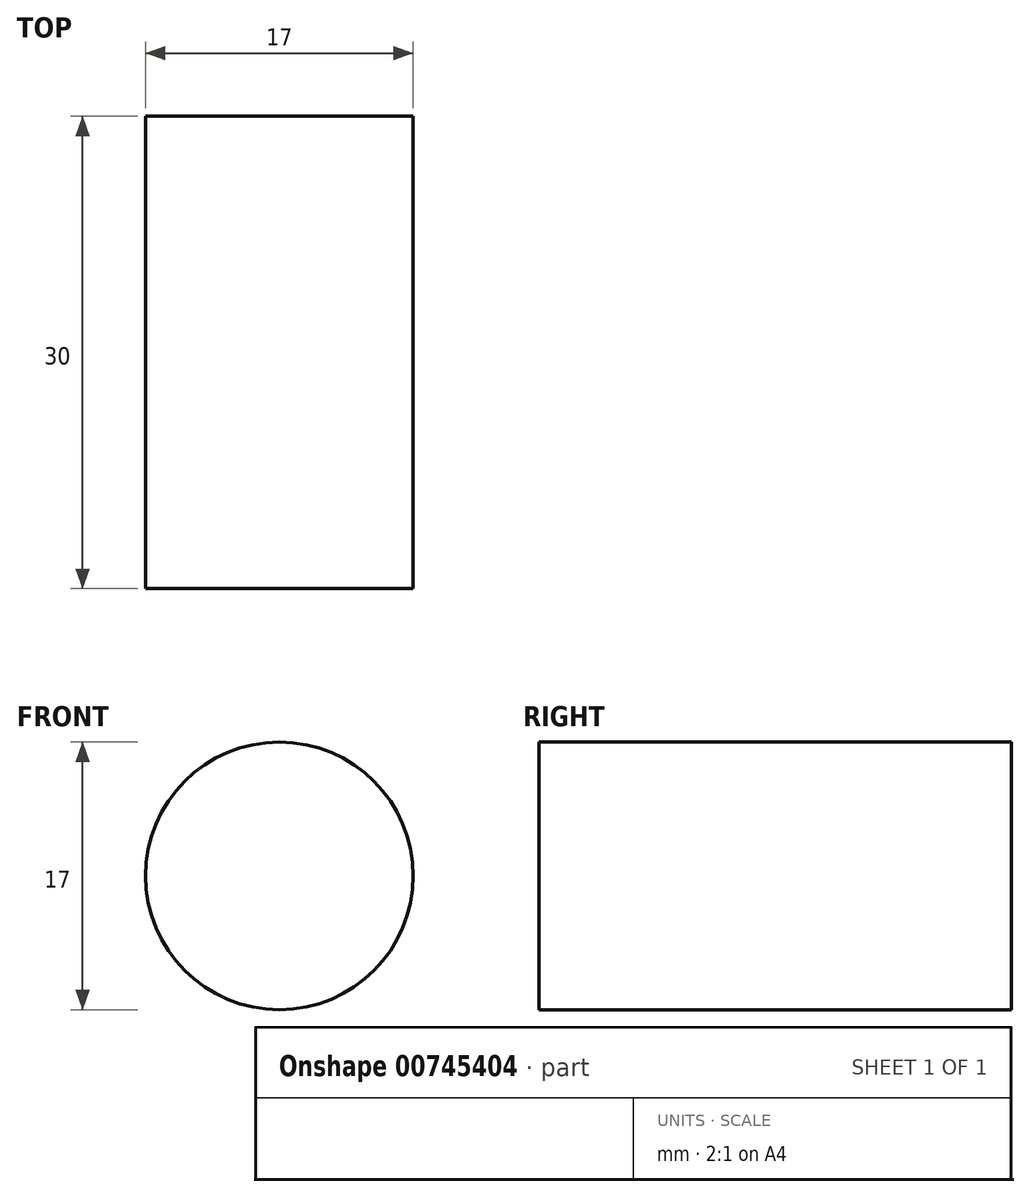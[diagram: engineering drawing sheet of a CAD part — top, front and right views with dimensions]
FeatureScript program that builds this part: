
annotation { "Feature Type Name" : "Feature", "Feature Type Description" : "" }
export const myFeature = defineFeature(function(context is Context, id is Id, definition is map)
    precondition{}
    {
        {
            var Q0;
            Q0=qCreatedBy(makeId("Front.planeOp"),FACE);
            var sketch = newSketch(context, id + "F0", { "sketchPlane" : qUnion([Q0])});
            skCircle(sketch, "E0", {"center": v(0, 0) * mm, "radius": 8.5 * mm});
            skLineSegment(sketch, "E1", {"start": v(0, 0) * mm, "end": v(100, 0) * mm, "construction": true});
            skSolve(sketch);
        }
        {
            var Q0;
            Q0 = qSketchRegion(id + "F0", true);
            extrude(context, id + "F1", {"entities" : qUnion([Q0]), "endBound" : BoundingType.SYMMETRIC, "depth" : 60 * mm, "offsetDistance" : 25 * mm});
        }
        {
            var Q0;
            Q0=qCreatedBy(makeId("Front.planeOp"),FACE);
            var sketch = newSketch(context, id + "F2", { "sketchPlane" : qUnion([Q0])});
            skCircle(sketch, "E2", {"center": v(0, 0) * mm, "radius": 13.32 * mm});
            skSolve(sketch);
        }
        {
            var Q0;
            Q0=makeQuery(id+"F2.imprint","IMPRINT",FACE,{"disambiguationData":[TD([[makeQuery(id+"F2.imprint","IMPRINT",EDGE,{"derivedFrom":sQuery(id+"F2.wireOp",EDGE,"E2")}),1.0]])]});
            var Q1;
            Q1=sQuery(id+"F2.wireOp",EDGE,"E2");
            extrude(context, id + "F3", {"entities" : qUnion([Q0]), "operationType" : NewBodyOperationType.REMOVE, "surfaceEntities" : qUnion([Q1]), "oppositeDirection" : true, "depth" : 39.4 * mm, "offsetDistance" : 25 * mm});
        }
    });
